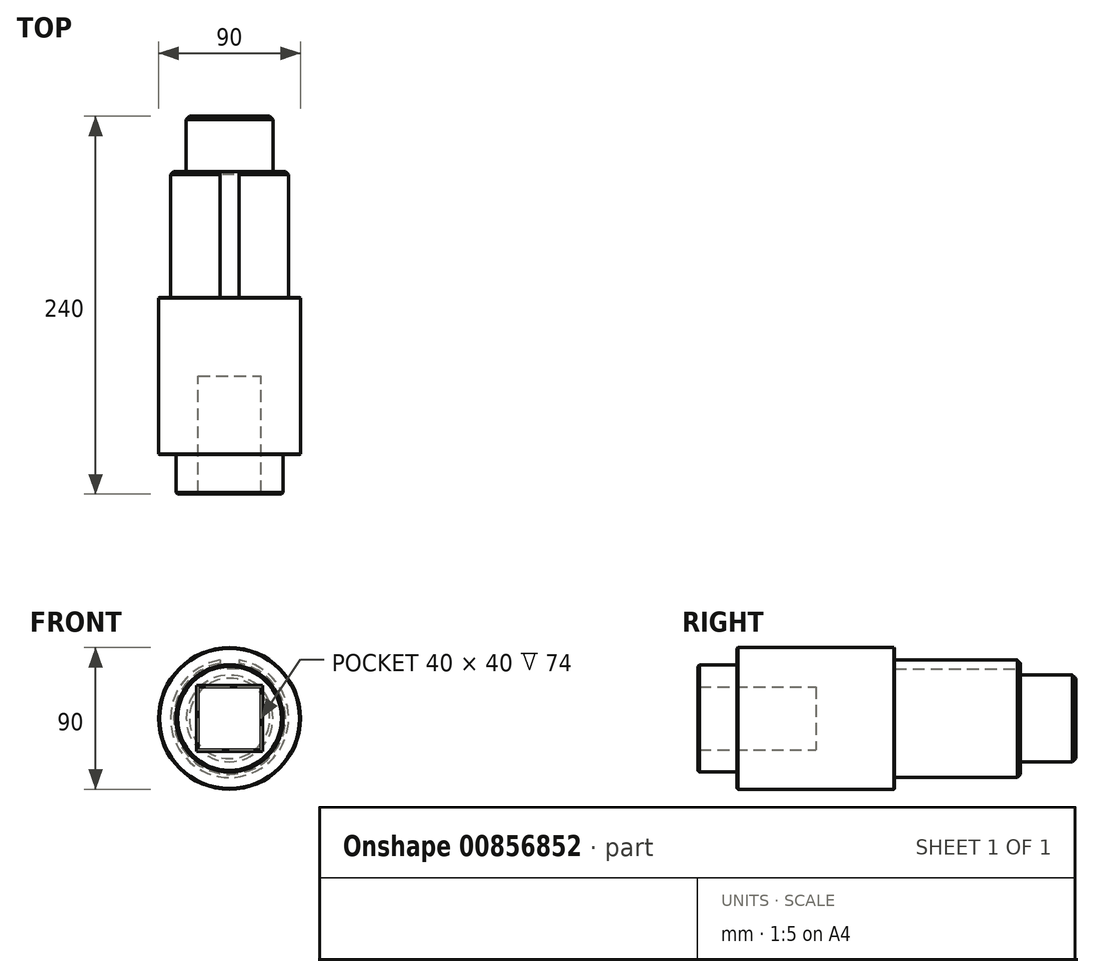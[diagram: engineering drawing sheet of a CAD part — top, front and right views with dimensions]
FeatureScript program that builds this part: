
annotation { "Feature Type Name" : "Feature", "Feature Type Description" : "" }
export const myFeature = defineFeature(function(context is Context, id is Id, definition is map)
    precondition{}
    {
        {
            var Q0;
            Q0=qCreatedBy(makeId("Front.planeOp"),FACE);
            var sketch = newSketch(context, id + "F0", { "sketchPlane" : qUnion([Q0])});
            skCircle(sketch, "E0", {"center": v(0, 0) * mm, "radius": 45 * mm});
            skLineSegment(sketch, "E1.bottom", {"start": v(20, -20) * mm, "end": v(-20, -20) * mm});
            skLineSegment(sketch, "E1.top", {"start": v(20, 20) * mm, "end": v(-20, 20) * mm});
            skLineSegment(sketch, "E1.left", {"start": v(20, -20) * mm, "end": v(20, 20) * mm});
            skLineSegment(sketch, "E1.right", {"start": v(-20, -20) * mm, "end": v(-20, 20) * mm});
            skSolve(sketch);
        }
        {
            var Q0;
            Q0 = qSketchRegion(id + "F0", true);
            extrude(context, id + "F1", {"entities" : qUnion([Q0]), "depth" : 100 * mm, "offsetDistance" : 25 * mm});
        }
        {
            var Q0;
            Q0=makeQuery(id+"F1.opExtrude","CAP_FACE",FACE,{"disambiguationData":[OSD([sQuery(id+"F0.wireOp",EDGE,"E0"),sQuery(id+"F0.wireOp",EDGE,"E1.bottom"),sQuery(id+"F0.wireOp",EDGE,"E1.top"),sQuery(id+"F0.wireOp",EDGE,"E1.left"),sQuery(id+"F0.wireOp",EDGE,"E1.right")])],"isStart":false});
            var sketch = newSketch(context, id + "F2", { "sketchPlane" : qUnion([Q0])});
            skLineSegment(sketch, "E2.bottom", {"start": v(20, 20) * mm, "end": v(-20, 20) * mm});
            skLineSegment(sketch, "E2.top", {"start": v(20, -20) * mm, "end": v(-20, -20) * mm});
            skLineSegment(sketch, "E2.left", {"start": v(20, 20) * mm, "end": v(20, -20) * mm});
            skLineSegment(sketch, "E2.right", {"start": v(-20, 20) * mm, "end": v(-20, -20) * mm});
            skPoint(sketch, "E2.middle", {"position": v(0, 0) * mm});
            skCircle(sketch, "E3", {"center": v(0, 0) * mm, "radius": 34 * mm});
            skSolve(sketch);
        }
        {
            var Q0;
            Q0 = qSketchRegion(id + "F2", true);
            extrude(context, id + "F3", {"entities" : qUnion([Q0]), "operationType" : NewBodyOperationType.ADD, "depth" : 25 * mm, "offsetDistance" : 25 * mm});
        }
        {
            var Q0;
            Q0=makeQuery(id+"F1.opExtrude","CAP_FACE",FACE,{"disambiguationData":[OSD([sQuery(id+"F0.wireOp",EDGE,"E0"),sQuery(id+"F0.wireOp",EDGE,"E1.bottom"),sQuery(id+"F0.wireOp",EDGE,"E1.top"),sQuery(id+"F0.wireOp",EDGE,"E1.left"),sQuery(id+"F0.wireOp",EDGE,"E1.right")])],"isStart":true});
            var sketch = newSketch(context, id + "F4", { "sketchPlane" : qUnion([Q0])});
            skCircle(sketch, "E4", {"center": v(0, 0) * mm, "radius": 37.5 * mm});
            skSolve(sketch);
        }
        {
            var Q0;
            Q0 = qSketchRegion(id + "F4", true);
            extrude(context, id + "F5", {"entities" : qUnion([Q0]), "operationType" : NewBodyOperationType.ADD, "depth" : 80 * mm, "offsetDistance" : 25 * mm, "hasSecondDirection" : true, "secondDirectionOppositeDirection" : true, "secondDirectionDepth" : 50 * mm});
        }
        {
            var Q0;
            {var subQ0=sQuery(id+"F4.wireOp",EDGE,"E4");Q0=makeQuery(id+"FM1HZRj7TIbd1aB_1.1.F8.boolean.opBoolean","SPLIT",EDGE,{"disambiguationData":[TD([makeQuery(id+"F8.boolean.opBoolean","COPY",FACE,{"derivedFrom":makeQuery(id+"F8.opExtrude","SWEPT_FACE",FACE,{"disambiguationData":[OSD([sQuery(id+"F7.wireOp",EDGE,"E6.left")])]})})])],"derivedFrom":makeQuery(id+"F5.opExtrude","CAP_EDGE",EDGE,{"disambiguationData":[OSD([subQ0])],"isStart":false})});}
            chamfer(context, id + "F6", {"entities" : qUnion([Q0]), "width" : 2 * mm, "tangentPropagation" : true});
        }
        {
            var Q0;
            Q0=makeQuery(id+"F5.opExtrude","CAP_FACE",FACE,{"disambiguationData":[OSD([sQuery(id+"F4.wireOp",EDGE,"E4")])],"isStart":false});
            var sketch = newSketch(context, id + "F7", { "sketchPlane" : qUnion([Q0])});
            skLineSegment(sketch, "E5", {"start": v(0, 0) * mm, "end": v(0, 37.5) * mm, "construction": true});
            skLineSegment(sketch, "E6.bottom", {"start": v(-6, 46.5) * mm, "end": v(6, 46.5) * mm});
            skLineSegment(sketch, "E6.top", {"start": v(-6, 31.5) * mm, "end": v(6, 31.5) * mm});
            skLineSegment(sketch, "E6.left", {"start": v(-6, 46.5) * mm, "end": v(-6, 31.5) * mm});
            skLineSegment(sketch, "E6.right", {"start": v(6, 46.5) * mm, "end": v(6, 31.5) * mm});
            skSolve(sketch);
        }
        {
            var Q0;
            Q0 = qSketchRegion(id + "F7", true);
            var Q1;
            Q1=makeQuery(id+"F1.opExtrude","CAP_FACE",FACE,{"disambiguationData":[OSD([sQuery(id+"F0.wireOp",EDGE,"E0"),sQuery(id+"F0.wireOp",EDGE,"E1.bottom"),sQuery(id+"F0.wireOp",EDGE,"E1.top"),sQuery(id+"F0.wireOp",EDGE,"E1.left"),sQuery(id+"F0.wireOp",EDGE,"E1.right")])],"isStart":true});
            extrude(context, id + "F8", {"entities" : qUnion([Q0]), "operationType" : NewBodyOperationType.REMOVE, "endBound" : BoundingType.UP_TO_SURFACE, "oppositeDirection" : true, "depth" : 25 * mm, "endBoundEntityFace" : qUnion([Q1]), "offsetDistance" : 25 * mm});
        }
        {
            var Q0;
            Q0=makeQuery(id+"F1.opExtrude","SWEPT_FACE",FACE,{"disambiguationData":[OSD([sQuery(id+"F0.wireOp",EDGE,"E0")])]});
            chamfer(context, id + "F9", {"entities" : qUnion([Q0]), "width" : 0.5 * mm, "tangentPropagation" : true});
        }
        {
            var Q0;
            Q0=makeQuery(id+"F5.opExtrude","CAP_FACE",FACE,{"disambiguationData":[OSD([sQuery(id+"F4.wireOp",EDGE,"E4")])],"isStart":false});
            var sketch = newSketch(context, id + "F10", { "sketchPlane" : qUnion([Q0])});
            skCircle(sketch, "E7", {"center": v(0, 0) * mm, "radius": 27.5 * mm});
            skSolve(sketch);
        }
        {
            var Q0;
            Q0 = qSketchRegion(id + "F10", true);
            extrude(context, id + "F11", {"entities" : qUnion([Q0]), "operationType" : NewBodyOperationType.ADD, "depth" : 35 * mm, "offsetDistance" : 25 * mm});
        }
        {
            var Q0;
            Q0=makeQuery(id+"F11.opExtrude","CAP_EDGE",EDGE,{"disambiguationData":[OSD([sQuery(id+"F10.wireOp",EDGE,"E7")])],"isStart":false});
            chamfer(context, id + "F12", {"entities" : qUnion([Q0]), "width" : 2 * mm, "tangentPropagation" : true});
        }
        {
            var Q0;
            Q0=makeQuery(id+"F3.opExtrude","CAP_FACE",FACE,{"disambiguationData":[OSD([sQuery(id+"F2.wireOp",EDGE,"E2.bottom"),sQuery(id+"F2.wireOp",EDGE,"E2.top"),sQuery(id+"F2.wireOp",EDGE,"E2.left"),sQuery(id+"F2.wireOp",EDGE,"E2.right"),sQuery(id+"F2.wireOp",EDGE,"E3")])],"isStart":false});
            chamfer(context, id + "F13", {"entities" : qUnion([Q0]), "width" : 1 * mm, "tangentPropagation" : true});
        }
    });
